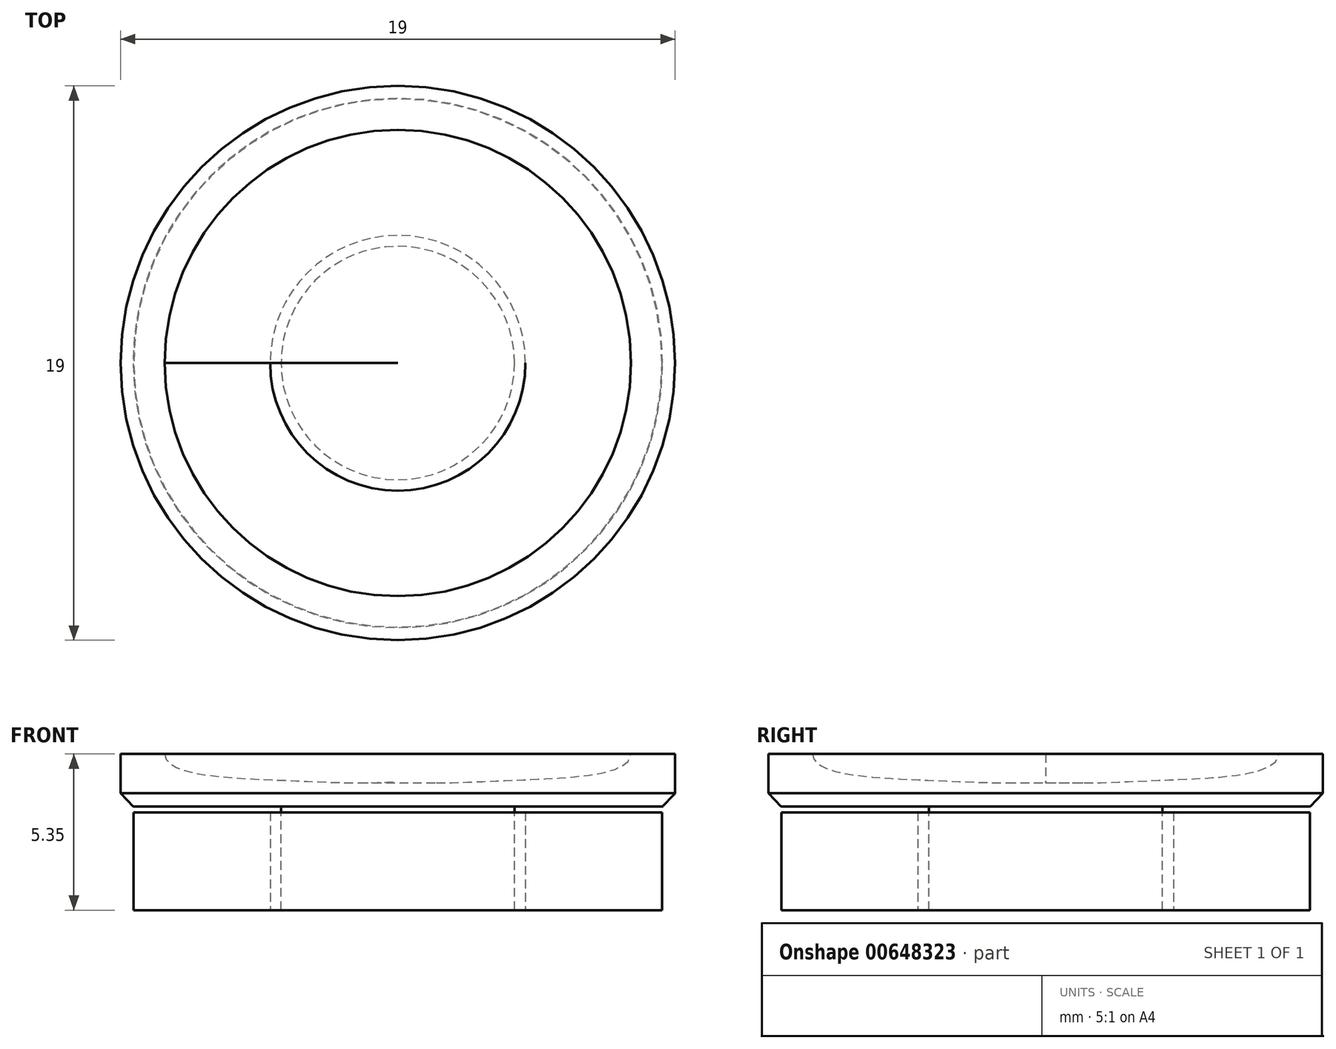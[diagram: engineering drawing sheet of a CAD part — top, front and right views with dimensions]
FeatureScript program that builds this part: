
annotation { "Feature Type Name" : "Feature", "Feature Type Description" : "" }
export const myFeature = defineFeature(function(context is Context, id is Id, definition is map)
    precondition{}
    {
        {
            var Q0;
            Q0=qCreatedBy(makeId("Front.planeOp"),FACE);
            var sketch = newSketch(context, id + "F0", { "sketchPlane" : qUnion([Q0])});
            skLineSegment(sketch, "E0", {"start": v(-9.5, 1.8) * mm, "end": v(-8, 1.8) * mm});
            skLineSegment(sketch, "E1", {"start": v(-9.5, 1.8) * mm, "end": v(-9.5, 0.45) * mm});
            skLineSegment(sketch, "E2", {"start": v(-9.07, 0) * mm, "end": v(0, 0) * mm});
            skLineSegment(sketch, "E3", {"start": v(-9.5, 0.45) * mm, "end": v(-9.07, 0) * mm});
            skFitSpline(sketch, "E4", {"points": [v(-8, 1.8) * mm, v(-4.15, 0.9) * mm, v(0, 0.85) * mm], "startDerivative": vector(0, -4.6) * mm, "endDerivative": vector(8.52, 0.54) * mm});
            skLineSegment(sketch, "E5", {"start": v(0, 0) * mm, "end": v(0, 0.85) * mm});
            skLineSegment(sketch, "E6", {"start": v(0, 2.4) * mm, "end": v(0, 0) * mm, "construction": true});
            skSolve(sketch);
        }
        {
            var Q0;
            Q0=qSketchRegion(id+"F0",true);
            var Q1;
            Q1=sQuery(id+"F0.wireOp",EDGE,"E6");
            revolve(context, id + "F1", {"entities" : qUnion([Q0]), "axis" : qUnion([Q1]), "revolveType" : RevolveType.FULL});
        }
        {
            var Q0;
            Q0=makeQuery(id+"F1.opRevolve","SWEPT_FACE",FACE,{"disambiguationData":[OSD([sQuery(id+"F0.wireOp",EDGE,"E2")])]});
            var sketch = newSketch(context, id + "F2", { "sketchPlane" : qUnion([Q0])});
            skCircle(sketch, "E7", {"center": v(0, 0) * mm, "radius": 4 * mm});
            skSolve(sketch);
        }
        {
            var Q0;
            Q0=makeQuery(id+"F2.imprint","IMPRINT",FACE,{"disambiguationData":[TD([[makeQuery(id+"F2.imprint","IMPRINT",EDGE,{"derivedFrom":sQuery(id+"F2.wireOp",EDGE,"E7")}),1.0]])]});
            extrude(context, id + "F3", {"entities" : qUnion([Q0]), "operationType" : NewBodyOperationType.ADD, "depth" : 3.55 * mm, "offsetDistance" : 25 * mm});
        }
        {
            var Q0;
            Q0=qCreatedBy(makeId("Top.planeOp"),FACE);
            cPlane(context, id + "F4", {"entities" : qUnion([Q0]), "cplaneType" : CPlaneType.OFFSET, "offset" : 3.55 * mm, "oppositeDirection" : true, "width" : 150 * mm, "height" : 150 * mm});
        }
        {
            var Q0;
            Q0=qCreatedBy(id+"F4.planeOp",FACE);
            var sketch = newSketch(context, id + "F5", { "sketchPlane" : qUnion([Q0])});
            skCircle(sketch, "E8", {"center": v(0, 0) * mm, "radius": 4.38 * mm});
            skCircle(sketch, "E9", {"center": v(0, 0) * mm, "radius": 9.05 * mm});
            skSolve(sketch);
        }
        {
            var Q0;
            Q0=makeQuery(id+"F5.imprint","IMPRINT",FACE,{"disambiguationData":[TD([[makeQuery(id+"F5.imprint","IMPRINT",EDGE,{"derivedFrom":sQuery(id+"F5.wireOp",EDGE,"E8")}),-1.0]])]});
            extrude(context, id + "F6", {"entities" : qUnion([Q0]), "depth" : 3.35 * mm, "offsetDistance" : 25 * mm});
        }
    });
